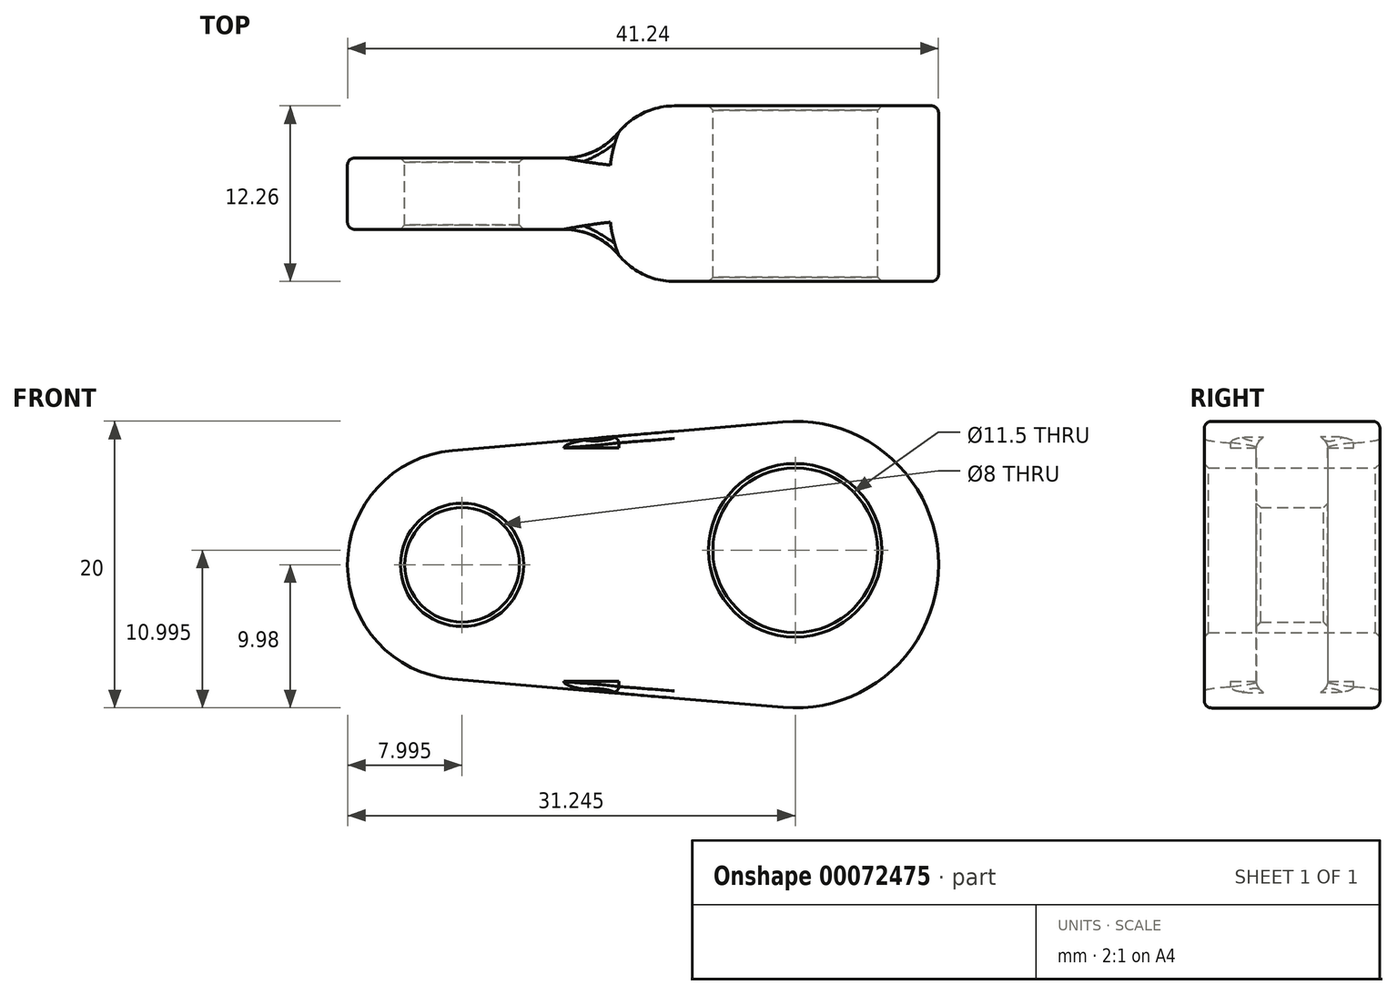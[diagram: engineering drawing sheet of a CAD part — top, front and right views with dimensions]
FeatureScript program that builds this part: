
annotation { "Feature Type Name" : "Feature", "Feature Type Description" : "" }
export const myFeature = defineFeature(function(context is Context, id is Id, definition is map)
    precondition{}
    {
        {
            var Q0;
            Q0=qCreatedBy(makeId("Front.planeOp"),FACE);
            var sketch = newSketch(context, id + "F0", { "sketchPlane" : qUnion([Q0])});
            skCircle(sketch, "E0", {"center": v(-11.62, 0) * mm, "radius": 4 * mm});
            skCircle(sketch, "E1", {"center": v(-11.62, 0) * mm, "radius": 8 * mm});
            skLineSegment(sketch, "E2", {"start": v(11.62, 1.02) * mm, "end": v(11.62, 0.02) * mm, "construction": true});
            skCircle(sketch, "E3", {"center": v(11.62, 0.02) * mm, "radius": 10 * mm});
            skLineSegment(sketch, "E4", {"start": v(-12.32, 7.97) * mm, "end": v(10.76, 9.98) * mm});
            skLineSegment(sketch, "E5", {"start": v(-12.3, -7.97) * mm, "end": v(10.77, -9.95) * mm});
            skLineSegment(sketch, "E6", {"start": v(0, 0) * mm, "end": v(-19.62, 0) * mm, "construction": true});
            skCircle(sketch, "E7", {"center": v(11.62, 1.02) * mm, "radius": 5.75 * mm});
            skSolve(sketch);
        }
        {
            var Q0;
            Q0=makeQuery(id+"F0.imprint","IMPRINT",FACE,{"disambiguationData":[TD([[makeQuery(id+"F0.imprint","IMPRINT",EDGE,{"derivedFrom":sQuery(id+"F0.wireOp",EDGE,"E0")}),-1.0]])]});
            var Q1;
            {var subQ0=sQuery(id+"F0.wireOp",EDGE,"E4");Q1=makeQuery(id+"F0.imprint","IMPRINT",FACE,{"disambiguationData":[TD([[makeQuery(id+"F0.imprint","IMPRINT",EDGE,{"derivedFrom":subQ0}),-1.0]])]});}
            var Q2;
            Q2=makeQuery(id+"F0.imprint","IMPRINT",FACE,{"disambiguationData":[TD([[makeQuery(id+"F0.imprint","IMPRINT",EDGE,{"derivedFrom":sQuery(id+"F0.wireOp",EDGE,"3260dc27-5993-441e-bcc4-bb6a67217cda0.MirrorC")}),1.0]])]});
            var Q3;
            Q3=makeQuery(id+"F0.imprint","IMPRINT",FACE,{"disambiguationData":[TD([[makeQuery(id+"F0.imprint","IMPRINT",EDGE,{"derivedFrom":sQuery(id+"F0.wireOp",EDGE,"E7")}),-1.0]])]});
            extrude(context, id + "F1", {"entities" : qUnion([Q0, Q1, Q2, Q3]), "depth" : 12.25 * mm, "symmetric" : true});
        }
        {
            var Q0;
            Q0=qCreatedBy(makeId("Right.planeOp"),FACE);
            cPlane(context, id + "F2", {"entities" : qUnion([Q0]), "cplaneType" : CPlaneType.OFFSET, "offset" : 21.62 * mm, "oppositeDirection" : true, "width" : 150 * mm, "height" : 150 * mm});
        }
        {
            var Q0;
            Q0=qCreatedBy(id+"F2.planeOp",FACE);
            var sketch = newSketch(context, id + "F3", { "sketchPlane" : qUnion([Q0])});
            skLineSegment(sketch, "E8", {"start": v(0, 0) * mm, "end": v(2.5, 0) * mm, "construction": true});
            skLineSegment(sketch, "E9.bottom", {"start": v(2.5, 0) * mm, "end": v(6.36, 0) * mm});
            skLineSegment(sketch, "E9.top", {"start": v(2.5, 10.87) * mm, "end": v(6.36, 10.87) * mm});
            skLineSegment(sketch, "E9.left", {"start": v(2.5, 0) * mm, "end": v(2.5, 10.87) * mm});
            skLineSegment(sketch, "E9.right", {"start": v(6.36, 0) * mm, "end": v(6.36, 10.87) * mm});
            skLineSegment(sketch, "E10.MirrorCS", {"start": v(-6.36, 0) * mm, "end": v(-6.36, 10.87) * mm});
            skLineSegment(sketch, "E11.MirrorCS", {"start": v(-2.5, 10.87) * mm, "end": v(-6.36, 10.87) * mm});
            skLineSegment(sketch, "E12.MirrorCS", {"start": v(-2.5, 0) * mm, "end": v(-2.5, 10.87) * mm});
            skLineSegment(sketch, "E13.MirrorCS", {"start": v(6.36, 0) * mm, "end": v(6.36, -10.87) * mm});
            skLineSegment(sketch, "E14.MirrorCS", {"start": v(2.5, -10.87) * mm, "end": v(6.36, -10.87) * mm});
            skLineSegment(sketch, "E15.MirrorCS", {"start": v(2.5, 0) * mm, "end": v(2.5, -10.87) * mm});
            skLineSegment(sketch, "E16.MirrorCS", {"start": v(-2.5, -10.87) * mm, "end": v(-6.36, -10.87) * mm});
            skLineSegment(sketch, "E17.MirrorCS", {"start": v(-2.5, 0) * mm, "end": v(-2.5, -10.87) * mm});
            skLineSegment(sketch, "E18.MirrorCS", {"start": v(-6.36, 0) * mm, "end": v(-6.36, -10.87) * mm});
            skSolve(sketch);
        }
        {
            var Q0;
            Q0=makeQuery(id+"F3.imprint","IMPRINT",FACE,{"disambiguationData":[TD([[makeQuery(id+"F3.imprint","IMPRINT",EDGE,{"derivedFrom":sQuery(id+"F3.wireOp",EDGE,"E9.bottom")}),1.0]])]});
            var Q1;
            Q1=makeQuery(id+"F3.imprint","IMPRINT",FACE,{"disambiguationData":[TD([[makeQuery(id+"F3.imprint","IMPRINT",EDGE,{"derivedFrom":sQuery(id+"F3.wireOp",EDGE,"E9.bottom")}),-1.0]])]});
            var Q2;
            Q2=makeQuery(id+"F3.imprint","IMPRINT",FACE,{"disambiguationData":[TD([[makeQuery(id+"F3.imprint","IMPRINT",EDGE,{"derivedFrom":sQuery(id+"F3.wireOp",EDGE,"E10.MirrorCS")}),-1.0]])]});
            extrude(context, id + "F4", {"entities" : qUnion([Q0, Q1, Q2]), "operationType" : NewBodyOperationType.REMOVE, "depth" : 20 * mm});
        }
        {
            var Q0;
            Q0=makeQuery(id+"F4.boolean.opBoolean","INTERSECT",EDGE,{"derivedFrom":[makeQuery(id+"F1.opExtrude","CAP_FACE",FACE,{"disambiguationData":[OSD([sQuery(id+"F0.wireOp",EDGE,"E0"),sQuery(id+"F0.wireOp",EDGE,"3260dc27-5993-441e-bcc4-bb6a67217cda0.MirrorC"),sQuery(id+"F0.wireOp",EDGE,"E1"),sQuery(id+"F0.wireOp",EDGE,"E3"),sQuery(id+"F0.wireOp",EDGE,"E4"),sQuery(id+"F0.wireOp",EDGE,"E5")])],"isStart":false}),makeQuery(id+"F4.opExtrude","CAP_FACE",FACE,{"disambiguationData":[OSD([sQuery(id+"F3.wireOp",EDGE,"E10.MirrorCS"),sQuery(id+"F3.wireOp",EDGE,"E11.MirrorCS"),sQuery(id+"F3.wireOp",EDGE,"E12.MirrorCS"),sQuery(id+"F3.wireOp",EDGE,"E16.MirrorCS"),sQuery(id+"F3.wireOp",EDGE,"E17.MirrorCS"),sQuery(id+"F3.wireOp",EDGE,"E18.MirrorCS")])],"isStart":false})]});
            var Q1;
            Q1=makeQuery(id+"F4.boolean.opBoolean","INTERSECT",EDGE,{"derivedFrom":[makeQuery(id+"F1.opExtrude","CAP_FACE",FACE,{"disambiguationData":[OSD([sQuery(id+"F0.wireOp",EDGE,"E0"),sQuery(id+"F0.wireOp",EDGE,"3260dc27-5993-441e-bcc4-bb6a67217cda0.MirrorC"),sQuery(id+"F0.wireOp",EDGE,"E1"),sQuery(id+"F0.wireOp",EDGE,"E3"),sQuery(id+"F0.wireOp",EDGE,"E4"),sQuery(id+"F0.wireOp",EDGE,"E5")])],"isStart":true}),makeQuery(id+"F4.opExtrude","CAP_FACE",FACE,{"disambiguationData":[OSD([sQuery(id+"F3.wireOp",EDGE,"E9.top"),sQuery(id+"F3.wireOp",EDGE,"E9.left"),sQuery(id+"F3.wireOp",EDGE,"E9.right"),sQuery(id+"F3.wireOp",EDGE,"E13.MirrorCS"),sQuery(id+"F3.wireOp",EDGE,"E14.MirrorCS"),sQuery(id+"F3.wireOp",EDGE,"E15.MirrorCS")])],"isStart":false})]});
            fillet(context, id + "F5", {"entities" : qUnion([Q0, Q1]), "radius" : 5 * mm, "tangentPropagation" : true, "allowEdgeOverflow" : false});
        }
        {
            var Q0;
            Q0=makeQuery(id+"F1.opExtrude","SWEPT_FACE",FACE,{"disambiguationData":[OSD([sQuery(id+"F0.wireOp",EDGE,"E0")])]});
            var Q1;
            Q1=makeQuery(id+"F1.opExtrude","SWEPT_FACE",FACE,{"disambiguationData":[OSD([sQuery(id+"F0.wireOp",EDGE,"3260dc27-5993-441e-bcc4-bb6a67217cda0.MirrorC")])]});
            var Q2;
            Q2=makeQuery(id+"F1.opExtrude","SWEPT_FACE",FACE,{"disambiguationData":[OSD([sQuery(id+"F0.wireOp",EDGE,"E7")])]});
            chamfer(context, id + "F6", {"entities" : qUnion([Q0, Q1, Q2]), "width" : .3 * mm, "tangentPropagation" : true});
        }
        {
            var Q0;
            Q0=makeQuery(id+"F1.opExtrude","SWEPT_FACE",FACE,{"disambiguationData":[OSD([sQuery(id+"F0.wireOp",EDGE,"E4")])]});
            fillet(context, id + "F7", {"entities" : qUnion([Q0]), "radius" : .5 * mm, "tangentPropagation" : true, "allowEdgeOverflow" : false});
        }
        {
            var Q0;
            {var subQ0=sQuery(id+"F3.wireOp",EDGE,"E15.MirrorCS");var subQ1=sQuery(id+"F3.wireOp",EDGE,"E9.left");Q0=makeQuery(id+"F5.opFillet","BLEND_EDGE",EDGE,{"blendedFrom":[makeQuery(id+"F4.boolean.opBoolean","INTERSECT",EDGE,{"derivedFrom":[makeQuery(id+"F1.opExtrude","CAP_FACE",FACE,{"disambiguationData":[OSD([sQuery(id+"F0.wireOp",EDGE,"E0"),sQuery(id+"F0.wireOp",EDGE,"E1"),sQuery(id+"F0.wireOp",EDGE,"E3"),sQuery(id+"F0.wireOp",EDGE,"E4"),sQuery(id+"F0.wireOp",EDGE,"E5"),sQuery(id+"F0.wireOp",EDGE,"E7")])],"isStart":true}),makeQuery(id+"F4.opExtrude","CAP_FACE",FACE,{"disambiguationData":[OSD([sQuery(id+"F3.wireOp",EDGE,"E9.top"),subQ1,sQuery(id+"F3.wireOp",EDGE,"E9.right"),sQuery(id+"F3.wireOp",EDGE,"E13.MirrorCS"),sQuery(id+"F3.wireOp",EDGE,"E14.MirrorCS"),subQ0])],"isStart":false})]}),makeQuery(id+"F4.boolean.opBoolean","COPY",FACE,{"derivedFrom":makeQuery(id+"F4.opExtrude","SWEPT_FACE",FACE,{"disambiguationData":[OSD([subQ1,subQ0])]})})],"blendedInto":[makeQuery(id+"F4.boolean.opBoolean","COPY",FACE,{"derivedFrom":makeQuery(id+"F4.opExtrude","SWEPT_FACE",FACE,{"disambiguationData":[OSD([subQ1,subQ0])]})})]});}
            var Q1;
            {var subQ0=sQuery(id+"F3.wireOp",EDGE,"E17.MirrorCS");var subQ1=sQuery(id+"F3.wireOp",EDGE,"E12.MirrorCS");Q1=makeQuery(id+"F5.opFillet","BLEND_EDGE",EDGE,{"blendedFrom":[makeQuery(id+"F4.boolean.opBoolean","INTERSECT",EDGE,{"derivedFrom":[makeQuery(id+"F1.opExtrude","CAP_FACE",FACE,{"disambiguationData":[OSD([sQuery(id+"F0.wireOp",EDGE,"E0"),sQuery(id+"F0.wireOp",EDGE,"E1"),sQuery(id+"F0.wireOp",EDGE,"E3"),sQuery(id+"F0.wireOp",EDGE,"E4"),sQuery(id+"F0.wireOp",EDGE,"E5"),sQuery(id+"F0.wireOp",EDGE,"E7")])],"isStart":false}),makeQuery(id+"F4.opExtrude","CAP_FACE",FACE,{"disambiguationData":[OSD([sQuery(id+"F3.wireOp",EDGE,"E10.MirrorCS"),sQuery(id+"F3.wireOp",EDGE,"E11.MirrorCS"),subQ1,sQuery(id+"F3.wireOp",EDGE,"E16.MirrorCS"),subQ0,sQuery(id+"F3.wireOp",EDGE,"E18.MirrorCS")])],"isStart":false})]}),makeQuery(id+"F4.boolean.opBoolean","COPY",FACE,{"derivedFrom":makeQuery(id+"F4.opExtrude","SWEPT_FACE",FACE,{"disambiguationData":[OSD([subQ1,subQ0])]})})],"blendedInto":[makeQuery(id+"F4.boolean.opBoolean","COPY",FACE,{"derivedFrom":makeQuery(id+"F4.opExtrude","SWEPT_FACE",FACE,{"disambiguationData":[OSD([subQ1,subQ0])]})})]});}
            fillet(context, id + "F8", {"entities" : qUnion([Q0, Q1]), "radius" : 5 * mm, "tangentPropagation" : true, "allowEdgeOverflow" : false});
        }
    });
